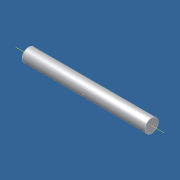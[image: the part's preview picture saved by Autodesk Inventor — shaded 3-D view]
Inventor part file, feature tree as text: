
AUTODESK INVENTOR PART (.ipt)
format: ipt  version: unknown  size: 154,112 bytes
history: native  units: mm
features: other x2, sketch x1
ambient origin geometry x8: Origin, YZ Plane, XZ Plane, XY Plane, X Axis, Y Axis, Z Axis, Center Point
feature tree (3):
  other  "stift.ipt"
  other  "Abgeleiteter Körper1"
  sketch  "Skizze1"  dims[d0=10.0mm]
